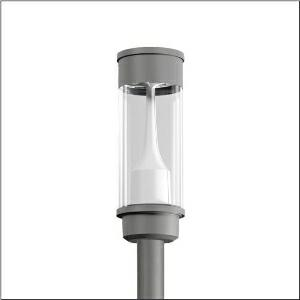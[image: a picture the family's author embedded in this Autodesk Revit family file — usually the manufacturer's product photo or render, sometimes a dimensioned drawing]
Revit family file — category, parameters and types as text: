
# Revit family: litepole_iq___p1_0a_5xa5415lf14hp_c39a
name_source: partatom
category: Lighting Fixtures
units: mm (PartAtom-declared; Revit-internal decimal feet)

## family parameters
Cut with Voids When Loaded = No
Host = Face
Light Source = No
Part Type = Normal
Room Calculation Point = No
Round Connector Dimension = Use Diameter
Shared = No

## types (1)
- --- (1 x LED, 4910 lm, 33.6 W, 4000K)
    Apparent Load = 34 VA
    CIE Flux Codes = 31 60 90 94 100
    Color Rendering = 70
    Color Temperature = 4000K
    Default Elevation = 1800 mm
    Description = Litepole iQ, mast luminaire, Module 540 iQ-SR, primary light control with 3 zone facetted reflector, of plastic, silver coated, highly specular, structured, primary optical cover: cover, of PMMA, transparent, partly coated, light distribution: P1.0a, light emission: direct distribution, primary light characteristic: strongly asymmetric, installation type: post-top, LED, High Power LED, rated luminous flux: 4.910lm, luminous efficacy: 146lm/W, light colour: 740, colour temperature: 4000K, control gear: iQ Street-Remote, control: optimised constant luminous flux control (CLO 2.0), Desk-Remote (wireless, voltage-free reading and setting of iQ features in the workshop via application-optimized NFC function/RFID function), Light-Fading, Smart-Wire, Night-Set, Lumen-Switch, Temp-Guard, Auto-Match, Street-Remote, pre-setting: logarithmic dimming characteristic, with terminal, 6-pole, max. 2.5mm², mains connection: 230..240V, AC, 50/60Hz, start of lifetime: 34W, end of service life: 36W, reduction: 15W, luminaire housing, upper part, of glass-fibre reinforced polyester, coated, Siteco® metallic grey (DB 702S), diameter: 210mm, height: 590mm, spigot size: d x l = 76 x 70mm (post-top) | with reducer (optional accessory) 60 x 70mm, mounting height: 3..5m, post-top mast mounting element, of diecast aluminium, coated, Siteco® metallic grey (DB 702S), Module 540 iQ-SR, traffic white (RAL 9016), equipment: Power, protection rating (complete): IP65, insulation class (complete): insulation class II (safety insulation), certification: CE, ENEC, VDE, packaging unit: 1 piece

Light Distribution: P1.0a
    Height = 590 mm
    Lamp = 1 x LED
    Lamp Light Flux = 4910 lm
    Lamp Power = 33.6 W
    Lamp count = 1
    Length = 220 mm
    Luminous efficacy = 146 lm/W
    Manufacturer = Siteco
    ModVariant = No
    Model = 5XA5415LF14HP
    Number of Poles = 1
    OnlyDefault = Yes
    Power Factor = 1
    Product Name = Litepole iQ | P1.0a
    Product group = mast luminaire | pylon top
    ProductGroupID = 6100
    Protection Class = Protection class II
    Protection Degree = IP 65
    RLX_Detail_Level = 1
    RLX_Emergency_Light_Flux = 0 lm
    RLX_Emergency_Type = 0
    RLX_Emergency_Type_DB = No
    RlxData = <blob elided: 29969 chars, md5=ae9a044d>
    Socket = socket
    Standby Power = 0 W
    System Light Flux = 4910 lm
    System Power = 34 W
    Type Comments = factory setting: luminous flux: 100 % | dim-lin: 254 | 695 mA
    Type Image = l_1006025.jpg
    URL = http://relux.com
    VarID = @adj_216197
    Voltage = 0 V
    Weight = 0.00 kg
    Width = 0 mm  [stored 0 ft]

note: [stored X ft] marks values corroborated as IEEE doubles in the binary element streams (Revit-internal decimal feet)

## geometry (parser evidence)
native form markers: Blend x4, Sweep x14
no freeform markers — native parametric forms only
